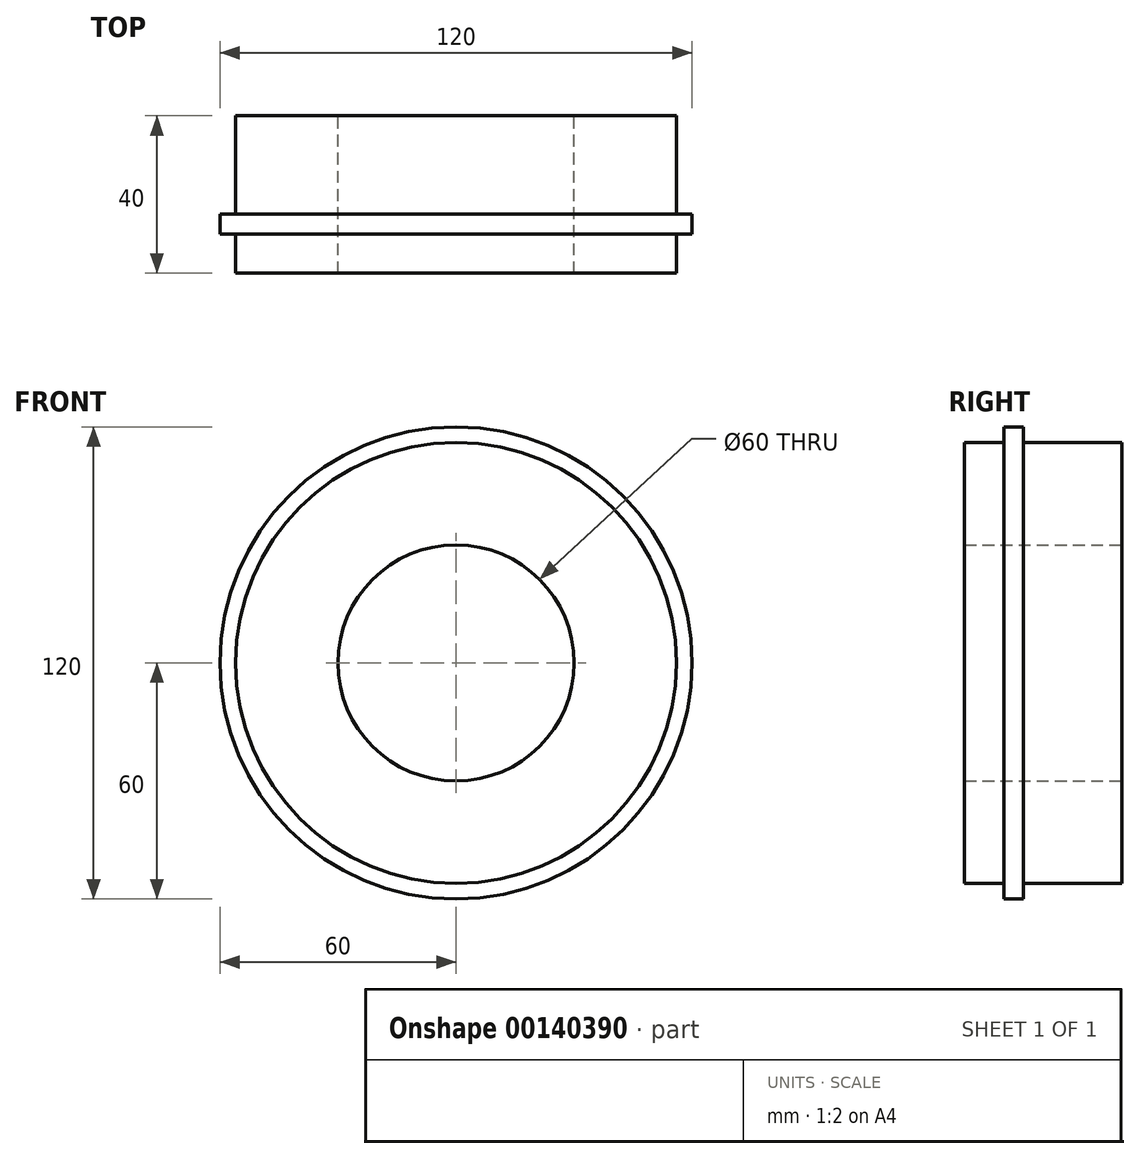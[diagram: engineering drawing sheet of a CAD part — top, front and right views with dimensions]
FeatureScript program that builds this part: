
annotation { "Feature Type Name" : "Feature", "Feature Type Description" : "" }
export const myFeature = defineFeature(function(context is Context, id is Id, definition is map)
    precondition{}
    {
        {
            var Q0;
            Q0=qCreatedBy(makeId("Right.planeOp"),FACE);
            var sketch = newSketch(context, id + "F0", { "sketchPlane" : qUnion([Q0])});
            skLineSegment(sketch, "E0.bottom", {"start": v(-20, 56) * mm, "end": v(20, 56) * mm});
            skLineSegment(sketch, "E0.top", {"start": v(-20, 30) * mm, "end": v(20, 30) * mm});
            skLineSegment(sketch, "E0.left", {"start": v(-20, 56) * mm, "end": v(-20, 30) * mm});
            skLineSegment(sketch, "E0.right", {"start": v(20, 56) * mm, "end": v(20, 30) * mm});
            skPoint(sketch, "E0.middle", {"position": v(0, 43) * mm});
            skLineSegment(sketch, "E1.bottom", {"start": v(-5, 56) * mm, "end": v(-10, 56) * mm});
            skLineSegment(sketch, "E1.top", {"start": v(-5, 60) * mm, "end": v(-10, 60) * mm});
            skLineSegment(sketch, "E1.left", {"start": v(-5, 56) * mm, "end": v(-5, 60) * mm});
            skLineSegment(sketch, "E1.right", {"start": v(-10, 56) * mm, "end": v(-10, 60) * mm});
            skLineSegment(sketch, "E2", {"start": v(74.17, 0) * mm, "end": v(-76.7, 0) * mm});
            skSolve(sketch);
        }
        {
            var Q0;
            Q0 = qSketchRegion(id + "F0", true);
            var Q1;
            Q1=sQuery(id+"F0.wireOp",EDGE,"E2");
            revolve(context, id + "F1", {"entities" : qUnion([Q0]), "axis" : qUnion([Q1]), "revolveType" : RevolveType.FULL});
        }
    });
